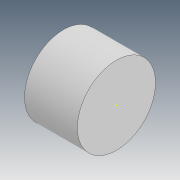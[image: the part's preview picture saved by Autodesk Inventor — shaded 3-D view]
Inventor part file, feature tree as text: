
AUTODESK INVENTOR PART (.ipt)
format: ipt  version: 2021 (Build 250183000, 183)  size: 115,200 bytes
history: native  units: in
note: dims shown in document units (in); Inventor stores cm internally (conversion verified against a paired STEP export)
features: sketch x7, extrude x4, other x2
ambient origin geometry x8: Origin, YZ Plane, XZ Plane, XY Plane, X Axis, Y Axis, Z Axis, Center Point
bodies: Body1 (feature_tree)
feature tree (13):
  other  "Sólido1"
  other  "Revolução1"
  extrude  "Extrusão1"  Depth=0.2618in
  extrude  "Extrusão2"  Depth=0.0984in
  sketch  "Esboço4"  dims[d6=0.0591in d7=0.0in d8=0.1181in]
  sketch  "Esboço5"  dims[d9=0.1575in d10=0.0in]
  extrude  "Extrusão3"  Depth=0.1575in
  extrude  "Extrusão4"  Depth=0.0591in
  sketch  "Esboço1"  dims[d0=0.3543in d1=0.2618in]
  sketch  "Esboço2"  dims[d2=0.0787in d3=0.0984in]
  sketch  "Esboço3"  dims[d4=90.0deg d5=0.1575in]
  sketch  "Esboço6"  dims[d11=0.0787in]
  sketch  "Esboço7"  dims[d12=0.0417in d13=0.0in d14=0.0591in d15=0.0in]
